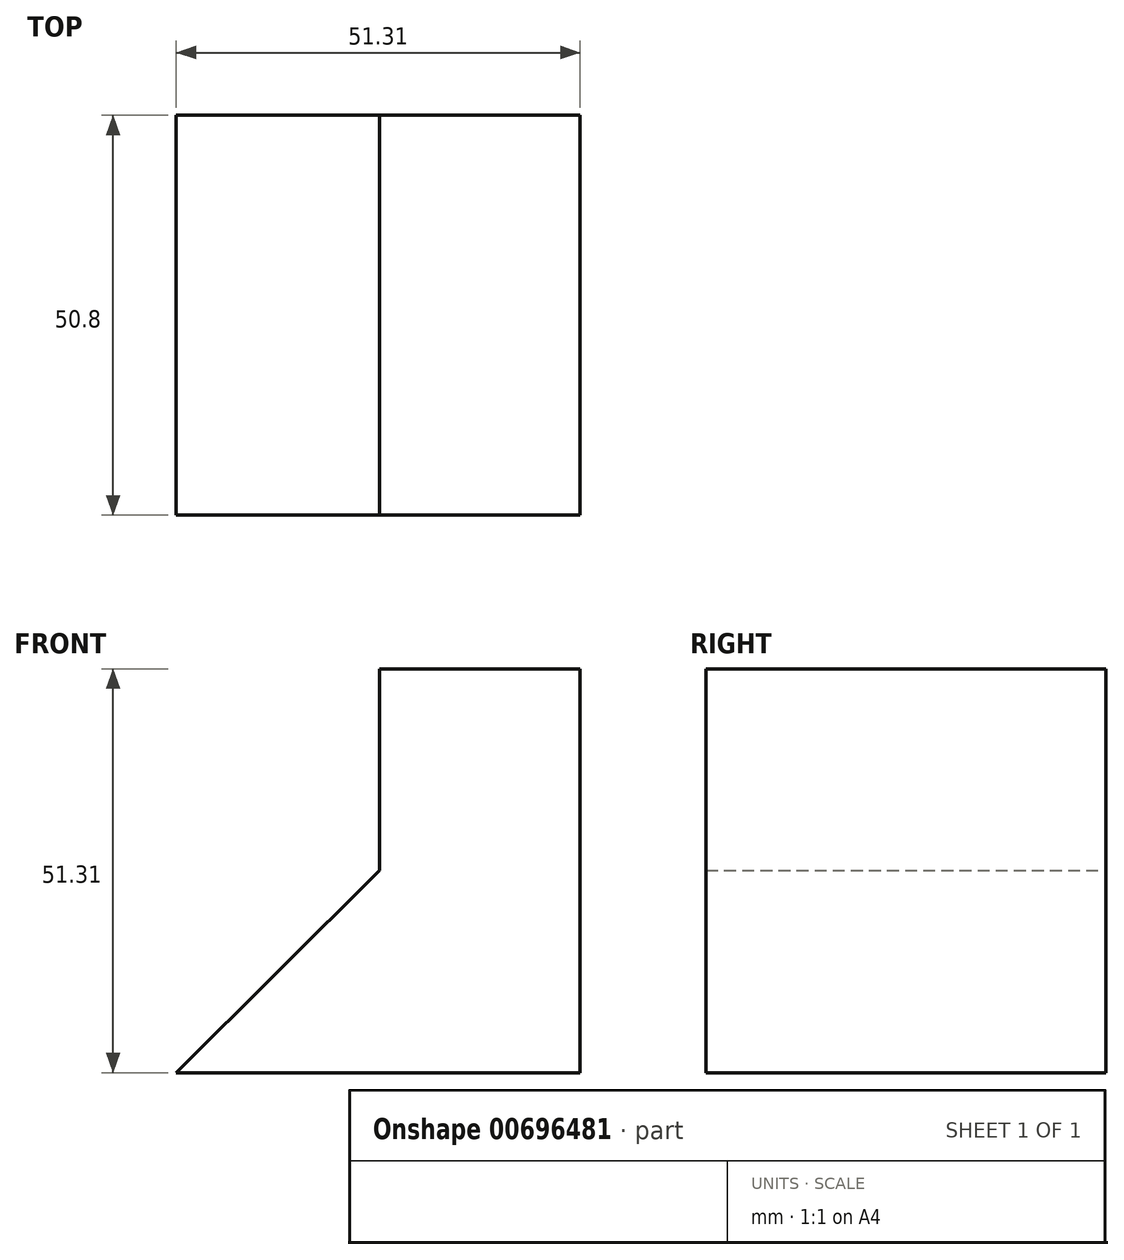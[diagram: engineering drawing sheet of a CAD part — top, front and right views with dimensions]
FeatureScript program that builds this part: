
annotation { "Feature Type Name" : "Feature", "Feature Type Description" : "" }
export const myFeature = defineFeature(function(context is Context, id is Id, definition is map)
    precondition{}
    {
        {
            var Q0;
            Q0=qCreatedBy(makeId("Front.planeOp"),FACE);
            var sketch = newSketch(context, id + "F0", { "sketchPlane" : qUnion([Q0])});
            skLineSegment(sketch, "E0", {"start": v(0, 0) * mm, "end": v(0, 51.3) * mm});
            skLineSegment(sketch, "E1", {"start": v(0, 0) * mm, "end": v(-51.3, 0) * mm});
            skLineSegment(sketch, "E2", {"start": v(0, 51.3) * mm, "end": v(-25.5, 51.3) * mm});
            skLineSegment(sketch, "E3", {"start": v(-25.5, 51.3) * mm, "end": v(-25.5, 25.7) * mm});
            skLineSegment(sketch, "E4", {"start": v(-25.5, 25.7) * mm, "end": v(-51.3, 0) * mm});
            skSolve(sketch);
        }
        {
            var Q0;
            Q0=makeQuery(id+"F0.imprint","IMPRINT",FACE,{"disambiguationData":[TD([[makeQuery(id+"F0.imprint","IMPRINT",EDGE,{"derivedFrom":sQuery(id+"F0.wireOp",EDGE,"E0")}),1.0]])]});
            extrude(context, id + "F1", {"entities" : qUnion([Q0]), "depth" : 50.8 * mm, "offsetDistance" : 25.4 * mm});
        }
    });
